# Revit family: Hager-WITTY EVOLUTIVE-en-NL
name_source: partatom
category: Electrical Fixtures
units: mm (PartAtom-declared; Revit-internal decimal feet)

## family parameters
Always vertical = Yes
Cut with Voids When Loaded = No
Host = Wall
Maintain Annotation Orientation = No
OmniClass Number = 23.80.00.00
OmniClass Title = Electric Power and Lighting
Part Type = Normal
Room Calculation Point = No
Round Connector Dimension = Use Diameter
Shared = No

## types (4) — shared parameters
Arrondi = 30 mm  [stored 0.0984252 ft]
BC_MODEL_ID = 1043723
BC_OBJECT_ID = 349819
BC_OBJECT_VERSION = #1
Code hager = ADD-EC002883_EVCS
Compatible with Amazon Alexa = No
Compatible with Apple HomeKit = No
Compatible with Google Assistant = No
Default Elevation = 1000 mm  [stored 3.28084 ft]
Degree of protection (IP) = IP55
Depth = 173 mm  [stored 0.567585 ft]
HG000003-Range = WITTY EVOLUTIVE
HG000059-Operating voltage = 410 V
HG000065-With socket TE = No
HG000099-Onfly Template ID = 1043713
Height = 549 mm  [stored 1.80118 ft]
Housing material = Plastic
IFTTT support available = No
Impact strength = IK10
Installation side connection model = 3-phase
Manufacturer = hager
Max. power per charging point = 22000 W
Mounting method = Wall mounting
Name = Template-EVCS-ParkEvolutive_EU-EC002883
Name BIM&CO = Workstation equipment
Name hager = ADD_ChargingStation_EC002883
Number of charging units = 1
Number of socket outlets Type 2 = 1
With display = No
With energy meter = No
With miniature circuit breaker (MCB) = No
zero-valued in all types: Length of charging cable, Number of CEE socket outlets, Number of earth leakage circuit breakers type A, Number of earth leakage circuit breakers type B, Number of household socket outlets, Number of socket outlets GB, Number of socket outlets Type 3, Number of vehicle connectors CHAdeMO, Number of vehicle connectors GB AC, Number of vehicle connectors GB DC, Number of vehicle connectors Type 1, Number of vehicle connectors Type 1 CCS, Number of vehicle connectors Type 2, Number of vehicle connectors Type 2 CCS

## per-type parameters (varying)
| type | BC_VARIANT_ID | Function access control | HG000004-Manufacturer reference | Nominal connection power | Reference description | Width | With communication interface | With house connection box | With load management |
| WITTY EVOLUTIVE-1x22KW-3P-XEV1K22T2S | 842279 | Yes | XEV1K22T2S | 0 W | EVSE witty solar 1x22kW 3P T2 + RFID | 251 mm | Yes | No | Yes |
| WITTY EVOLUTIVE-1x22KW-3P-XEV1K22T2SEMC | 842281 | Yes | XEV1K22T2SEMC | 0 W | KIT witty solar 22kW/RFID + EMC +PV3P | 251 mm | Yes | No | Yes |
| WITTY EVOLUTIVE-1x22KW-3P-XEV1R22T2 | 842282 | Yes | XEV1R22T2 | 11000 W | EVSE witty 1x22kW 3P T2 RFID | 237 mm  [stored 0.777559 ft] | No | Yes | Yes |
| WITTY EVOLUTIVE-1x22KW-3P-XEV1K11T2 | 842277 | No | XEV1K11T2 | 11000 W | EVSE witty 1x11/22kW 3P T2 with key | 251 mm | Yes | No | No |

note: column(s) folded — value = type name in every type: Reference

note: [stored X ft] marks values corroborated as IEEE doubles in the binary element streams (Revit-internal decimal feet)

## geometry (parser evidence)
native form markers: Sweep x3
no freeform markers — native parametric forms only
